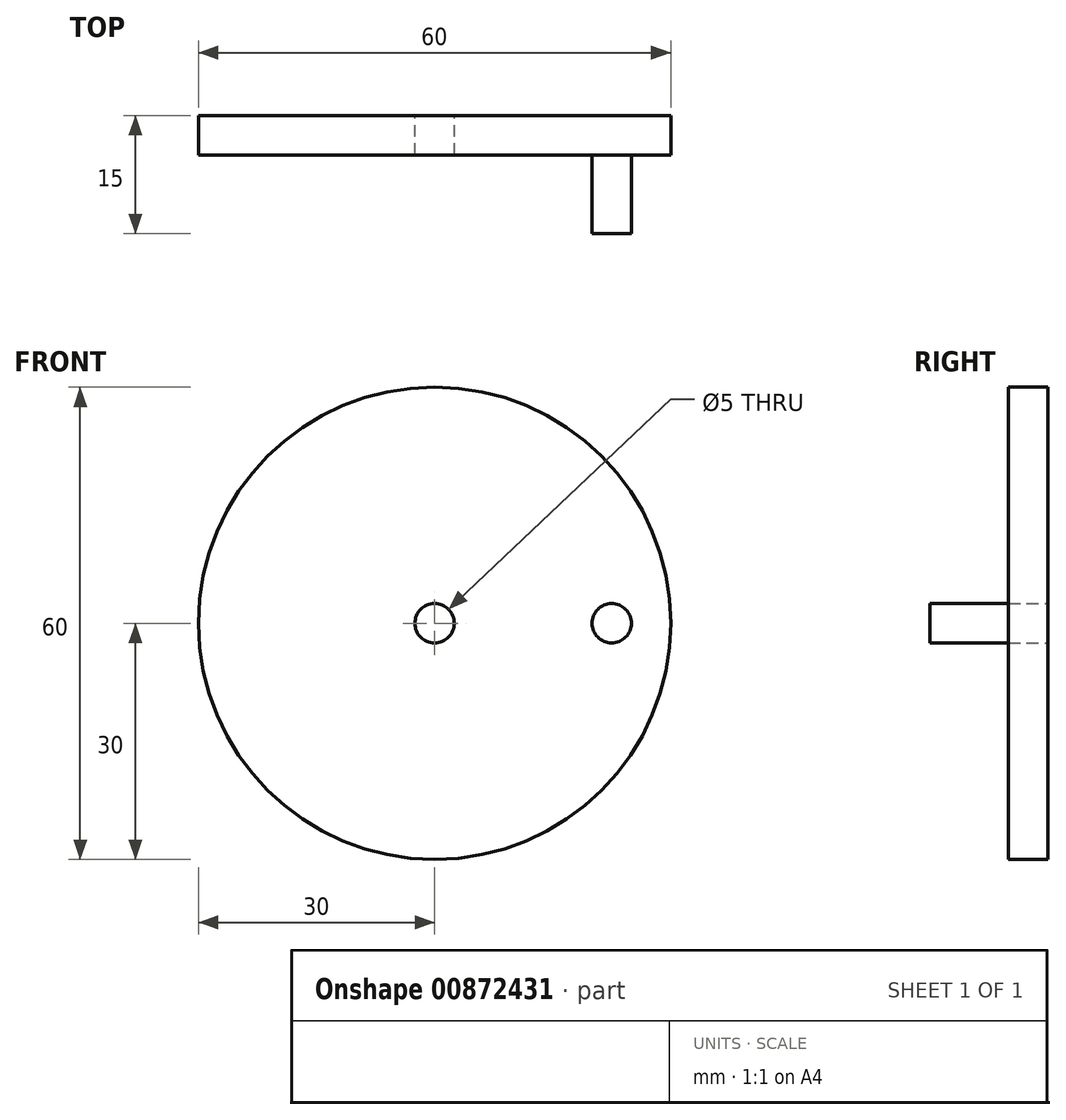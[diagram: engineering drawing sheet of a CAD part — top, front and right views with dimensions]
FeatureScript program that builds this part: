
annotation { "Feature Type Name" : "Feature", "Feature Type Description" : "" }
export const myFeature = defineFeature(function(context is Context, id is Id, definition is map)
    precondition{}
    {
        {
            var Q0;
            Q0=qCreatedBy(makeId("Front.planeOp"),FACE);
            var sketch = newSketch(context, id + "F0", { "sketchPlane" : qUnion([Q0])});
            skCircle(sketch, "E0", {"center": v(0, 0) * mm, "radius": 30 * mm});
            skCircle(sketch, "E1", {"center": v(0, 0) * mm, "radius": 2.5 * mm});
            skSolve(sketch);
        }
        {
            var Q0;
            Q0=makeQuery(id+"F0.imprint","IMPRINT",FACE,{"disambiguationData":[TD([[makeQuery(id+"F0.imprint","IMPRINT",EDGE,{"derivedFrom":sQuery(id+"F0.wireOp",EDGE,"E0")}),1.0]])]});
            var Q1;
            Q1=sQuery(id+"F0.wireOp",EDGE,"E0");
            extrude(context, id + "F1", {"entities" : qUnion([Q0]), "surfaceEntities" : qUnion([Q1]), "depth" : 5 * mm, "offsetDistance" : 25 * mm});
        }
        {
            var Q0;
            Q0=makeQuery(id+"F1.opExtrude","CAP_FACE",FACE,{"disambiguationData":[OSD([sQuery(id+"F0.wireOp",EDGE,"E0")])],"isStart":false});
            var sketch = newSketch(context, id + "F2", { "sketchPlane" : qUnion([Q0])});
            skCircle(sketch, "E2", {"center": v(22.5, 0) * mm, "radius": 2.5 * mm});
            skSolve(sketch);
        }
        {
            var Q0;
            Q0=makeQuery(id+"F2.imprint","IMPRINT",FACE,{"disambiguationData":[TD([[makeQuery(id+"F2.imprint","IMPRINT",EDGE,{"derivedFrom":sQuery(id+"F2.wireOp",EDGE,"E2")}),1.0]])]});
            var Q1;
            Q1=sQuery(id+"F2.wireOp",EDGE,"E2");
            extrude(context, id + "F3", {"entities" : qUnion([Q0]), "operationType" : NewBodyOperationType.ADD, "surfaceEntities" : qUnion([Q1]), "depth" : 10 * mm, "offsetDistance" : 25 * mm});
        }
    });
